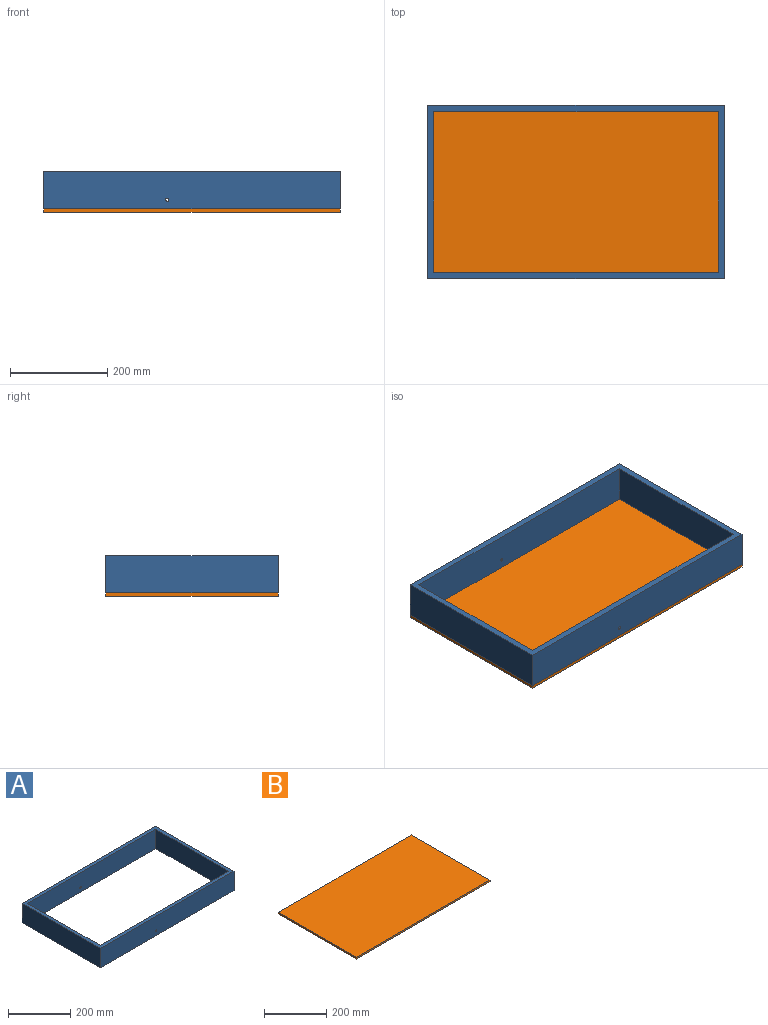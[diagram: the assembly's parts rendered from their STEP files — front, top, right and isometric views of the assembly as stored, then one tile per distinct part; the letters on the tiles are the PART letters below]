
ASSEMBLY  parts=2 mates=1
PART A: 12 faces, bbox 609.6x355.6x76.2 mm
  f0: plane 330.2x76.2mm, normal (1,0,0), area 25161.2mm2, adj f1,f7,f8,f9
  f1: plane 584.2x76.2mm, normal (0,-1,0), area 44484.4mm2, adj f0,f2,f8,f9,f11
  f2: plane 330.2x76.2mm, normal (-1,0,0), area 25161.2mm2, adj f1,f7,f8,f9
  f3: plane 355.6x76.2mm, normal (-1,0,0), area 27096.7mm2, adj f4,f6,f8,f9
  f4: plane 609.6x76.2mm, normal (0,-1,0), area 46419.9mm2, adj f3,f5,f8,f9,f10
  f5: plane 355.6x76.2mm, normal (1,0,0), area 27096.7mm2, adj f4,f6,f8,f9
  f6: plane 609.6x76.2mm, normal (0,1,0), area 46419.9mm2, adj f3,f5,f8,f9,f11
  f7: plane 584.2x76.2mm, normal (0,1,0), area 44484.4mm2, adj f0,f2,f8,f9,f10
  f8: plane 609.6x355.6mm, normal (0,0,1), area 23870.9mm2, adj f0,f1,f2,f3,f4,f5,f6,f7
  f9: plane 609.6x355.6mm, normal (0,0,-1), area 23870.9mm2, adj f0,f1,f2,f3,f4,f5,f6,f7
  f10: cylinder r=3.17mm len=12.7mm, axis (0,-1,0), area 253.4mm2, adj f4,f7
  f11: cylinder r=3.17mm len=12.7mm, axis (0,-1,0), area 253.4mm2, adj f1,f6
PART B: 6 faces, bbox 609.6x355.6x6.4 mm
  f0: plane 609.6x6.35mm, normal (0,-1,0), area 3871mm2, adj f1,f3,f4,f5
  f1: plane 355.6x6.35mm, normal (-1,0,0), area 2258.1mm2, adj f0,f2,f4,f5
  f2: plane 609.6x6.35mm, normal (0,1,0), area 3871mm2, adj f1,f3,f4,f5
  f3: plane 355.6x6.35mm, normal (1,0,0), area 2258.1mm2, adj f0,f2,f4,f5
  f4: plane 609.6x355.6mm, normal (0,0,-1), area 216773.8mm2, adj f0,f1,f2,f3
  f5: plane 609.6x355.6mm, normal (0,0,1), area 216773.8mm2, adj f0,f1,f2,f3
PLACE A at identity
PLACE B at identity fixed
MATE fastened B.f5 <-> A.f9  axis (0,0,1) through (0,0,0)mm
